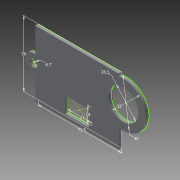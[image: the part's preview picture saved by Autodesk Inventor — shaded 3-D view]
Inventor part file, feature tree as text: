
AUTODESK INVENTOR PART (.ipt)
format: ipt  version: 2015 (Build 190159000, 159)  size: 125,952 bytes
history: native  units: mm
features: extrude x2, sketch x1
ambient origin geometry x8: Origin, YZ Plane, XZ Plane, XY Plane, X Axis, Y Axis, Z Axis, Center Point
bodies: Body1 (feature_tree)
feature tree (3):
  sketch  "Sketch1"  dims[d0=58.0mm d1=73.5mm d7=6.7mm d8=40.0mm d9=26.5mm d12=21.0mm d13=14.0mm d14=33.0mm d16=2.5mm d17=0.0mm d18=1.0mm d19=0.0mm]
  extrude  "Extrusion2"  Depth=73.5mm
  extrude  "Extrusion3"  Depth=1.0mm
